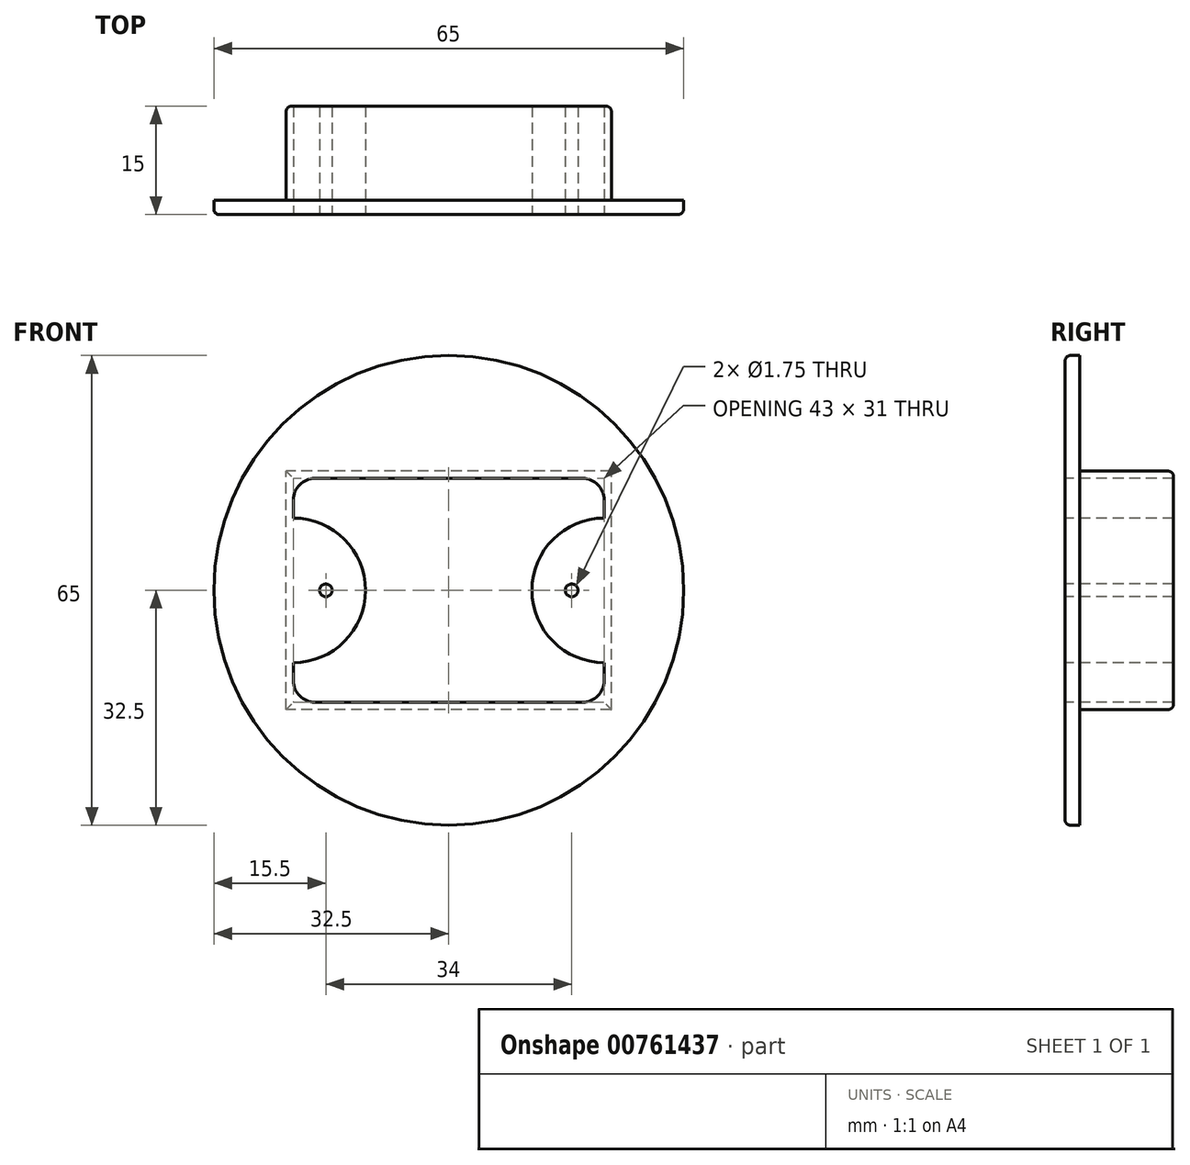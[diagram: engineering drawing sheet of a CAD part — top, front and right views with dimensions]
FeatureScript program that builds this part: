
annotation { "Feature Type Name" : "Feature", "Feature Type Description" : "" }
export const myFeature = defineFeature(function(context is Context, id is Id, definition is map)
    precondition{}
    {
        {
            var Q0;
            Q0=qCreatedBy(makeId("Front.planeOp"),FACE);
            var sketch = newSketch(context, id + "F0", { "sketchPlane" : qUnion([Q0])});
            skLineSegment(sketch, "E0.bottom", {"start": v(0, 0) * mm, "end": v(-45, 0) * mm});
            skLineSegment(sketch, "E0.top", {"start": v(0, 33) * mm, "end": v(-45, 33) * mm});
            skLineSegment(sketch, "E0.left", {"start": v(0, 0) * mm, "end": v(0, 33) * mm});
            skLineSegment(sketch, "E0.right", {"start": v(-45, 0) * mm, "end": v(-45, 33) * mm});
            skLineSegment(sketch, "E1.0", {"start": v(-4, 32) * mm, "end": v(-41, 32) * mm});
            skLineSegment(sketch, "E1.1", {"start": v(-1, 4) * mm, "end": v(-1, 29) * mm});
            skLineSegment(sketch, "E1.2", {"start": v(-4, 1) * mm, "end": v(-41, 1) * mm});
            skLineSegment(sketch, "E1.3", {"start": v(-44, 4) * mm, "end": v(-44, 29) * mm});
            skArc(sketch, "E2", {"start": v(-44, 6.5) * mm, "mid": v(-34, 16.5) * mm, "end": v(-44, 26.5) * mm});
            skPoint(sketch, "E3.firstSnap0", {"position": v(-22.5, 33) * mm});
            skPoint(sketch, "E3.oppositeSnap0", {"position": v(-22.5, 33) * mm});
            skLineSegment(sketch, "E3.bottom", {"start": v(-22.5, 47.86) * mm, "end": v(-22.5, 47.86) * mm});
            skLineSegment(sketch, "E3.top", {"start": v(-22.5, -13.6) * mm, "end": v(-22.5, -13.6) * mm});
            skLineSegment(sketch, "E3.left", {"start": v(-22.5, 47.86) * mm, "end": v(-22.5, -13.6) * mm, "construction": true});
            skLineSegment(sketch, "E3.right", {"start": v(-22.5, 47.86) * mm, "end": v(-22.5, -13.6) * mm, "construction": true});
            skArc(sketch, "E4", {"start": v(-1, 26.5) * mm, "mid": v(-11, 16.5) * mm, "end": v(-1, 6.5) * mm});
            skCircle(sketch, "E5", {"center": v(-39.5, 16.5) * mm, "radius": 0.88 * mm});
            skCircle(sketch, "E6", {"center": v(-5.5, 16.5) * mm, "radius": 0.88 * mm});
            skPoint(sketch, "E7", {"position": v(-22.5, 16.5) * mm});
            skCircle(sketch, "E8", {"center": v(-22.5, 16.5) * mm, "radius": 32.5 * mm});
            skLineSegment(sketch, "E9.bottom", {"start": v(-18.5, 1) * mm, "end": v(-26.5, 1) * mm});
            skLineSegment(sketch, "E9.top", {"start": v(-18.5, 32) * mm, "end": v(-26.5, 32) * mm});
            skLineSegment(sketch, "E9.left", {"start": v(-13.5, 6) * mm, "end": v(-13.5, 27) * mm});
            skLineSegment(sketch, "E9.right", {"start": v(-31.5, 6) * mm, "end": v(-31.5, 27) * mm});
            skPoint(sketch, "E10.visualSharp", {"position": v(-13.5, 32) * mm});
            skArc(sketch, "E10.filletArc", {"start": v(-13.5, 27) * mm, "mid": v(-14.96, 30.54) * mm, "end": v(-18.5, 32) * mm});
            skPoint(sketch, "E11.visualSharp", {"position": v(-31.5, 32) * mm});
            skArc(sketch, "E11.filletArc", {"start": v(-26.5, 32) * mm, "mid": v(-30.04, 30.54) * mm, "end": v(-31.5, 27) * mm});
            skPoint(sketch, "E12.visualSharp", {"position": v(-31.5, 1) * mm});
            skArc(sketch, "E12.filletArc", {"start": v(-31.5, 6) * mm, "mid": v(-30.04, 2.46) * mm, "end": v(-26.5, 1) * mm});
            skPoint(sketch, "E13.visualSharp", {"position": v(-13.5, 1) * mm});
            skArc(sketch, "E13.filletArc", {"start": v(-18.5, 1) * mm, "mid": v(-14.96, 2.46) * mm, "end": v(-13.5, 6) * mm});
            skPoint(sketch, "E14.visualSharp", {"position": v(-44, 32) * mm});
            skArc(sketch, "E14.filletArc", {"start": v(-41, 32) * mm, "mid": v(-43.12, 31.12) * mm, "end": v(-44, 29) * mm});
            skPoint(sketch, "E15.visualSharp", {"position": v(-44, 1) * mm});
            skArc(sketch, "E15.filletArc", {"start": v(-44, 4) * mm, "mid": v(-43.12, 1.88) * mm, "end": v(-41, 1) * mm});
            skPoint(sketch, "E16.visualSharp", {"position": v(-1, 32) * mm});
            skArc(sketch, "E16.filletArc", {"start": v(-1, 29) * mm, "mid": v(-1.88, 31.12) * mm, "end": v(-4, 32) * mm});
            skPoint(sketch, "E17.visualSharp", {"position": v(-1, 1) * mm});
            skArc(sketch, "E17.filletArc", {"start": v(-4, 1) * mm, "mid": v(-1.88, 1.88) * mm, "end": v(-1, 4) * mm});
            skSolve(sketch);
        }
        {
            var Q0;
            Q0=makeQuery(id+"F0.imprint","IMPRINT",FACE,{"disambiguationData":[TD([[makeQuery(id+"F0.imprint","IMPRINT",EDGE,{"derivedFrom":sQuery(id+"F0.wireOp",EDGE,"E0.bottom")}),1.0]])]});
            var Q1;
            {var subQ4=sQuery(id+"F0.wireOp",EDGE,"E4");Q1=makeQuery(id+"F0.imprint","IMPRINT",FACE,{"disambiguationData":[TD([[makeQuery(id+"F0.imprint","IMPRINT",EDGE,{"derivedFrom":subQ4}),-1.0]])]});}
            var Q2;
            {var subQ3=sQuery(id+"F0.wireOp",EDGE,"E2");Q2=makeQuery(id+"F0.imprint","IMPRINT",FACE,{"disambiguationData":[TD([[makeQuery(id+"F0.imprint","IMPRINT",EDGE,{"derivedFrom":subQ3}),-1.0]])]});}
            var Q3;
            Q3=makeQuery(id+"F0.imprint","IMPRINT",FACE,{"disambiguationData":[TD([[makeQuery(id+"F0.imprint","IMPRINT",EDGE,{"derivedFrom":sQuery(id+"F0.wireOp",EDGE,"E0.bottom")}),-1.0]])]});
            extrude(context, id + "F1", {"entities" : qUnion([Q0, Q1, Q2, Q3]), "oppositeDirection" : true, "depth" : 2 * mm, "offsetDistance" : 25 * mm});
        }
        {
            var Q0;
            Q0=makeQuery(id+"F0.imprint","IMPRINT",FACE,{"disambiguationData":[TD([[makeQuery(id+"F0.imprint","IMPRINT",EDGE,{"derivedFrom":sQuery(id+"F0.wireOp",EDGE,"E0.bottom")}),-1.0]])]});
            var Q1;
            {var subQ0=sQuery(id+"F0.wireOp",EDGE,"E4");Q1=makeQuery(id+"F0.imprint","IMPRINT",FACE,{"disambiguationData":[TD([[makeQuery(id+"F0.imprint","IMPRINT",EDGE,{"derivedFrom":subQ0}),1.0]])]});}
            var Q2;
            {var subQ0=sQuery(id+"F0.wireOp",EDGE,"E2");Q2=makeQuery(id+"F0.imprint","IMPRINT",FACE,{"disambiguationData":[TD([[makeQuery(id+"F0.imprint","IMPRINT",EDGE,{"derivedFrom":subQ0}),1.0]])]});}
            extrude(context, id + "F2", {"entities" : qUnion([Q0, Q1, Q2]), "operationType" : NewBodyOperationType.ADD, "oppositeDirection" : true, "depth" : 15 * mm, "offsetDistance" : 25 * mm});
        }
        {
            var Q0;
            Q0=makeQuery(id+"F1.opExtrude","CAP_EDGE",EDGE,{"disambiguationData":[OSD([sQuery(id+"F0.wireOp",EDGE,"E8")])],"isStart":true});
            fillet(context, id + "F3", {"entities" : qUnion([Q0]), "radius" : 0.75 * mm, "tangentPropagation" : true, "allowEdgeOverflow" : false});
        }
        {
            var Q0;
            Q0=makeQuery(id+"F2.opExtrude","CAP_EDGE",EDGE,{"disambiguationData":[OSD([sQuery(id+"F0.wireOp",EDGE,"E0.left")])],"isStart":false});
            var Q1;
            Q1=makeQuery(id+"F2.opExtrude","CAP_EDGE",EDGE,{"disambiguationData":[OSD([sQuery(id+"F0.wireOp",EDGE,"E0.top")])],"isStart":false});
            var Q2;
            Q2=makeQuery(id+"F2.opExtrude","CAP_EDGE",EDGE,{"disambiguationData":[OSD([sQuery(id+"F0.wireOp",EDGE,"E0.bottom")])],"isStart":false});
            var Q3;
            Q3=makeQuery(id+"F2.opExtrude","CAP_EDGE",EDGE,{"disambiguationData":[OSD([sQuery(id+"F0.wireOp",EDGE,"E0.right")])],"isStart":false});
            fillet(context, id + "F4", {"entities" : qUnion([Q0, Q1, Q2, Q3]), "radius" : 0.75 * mm, "tangentPropagation" : true, "allowEdgeOverflow" : false});
        }
    });
